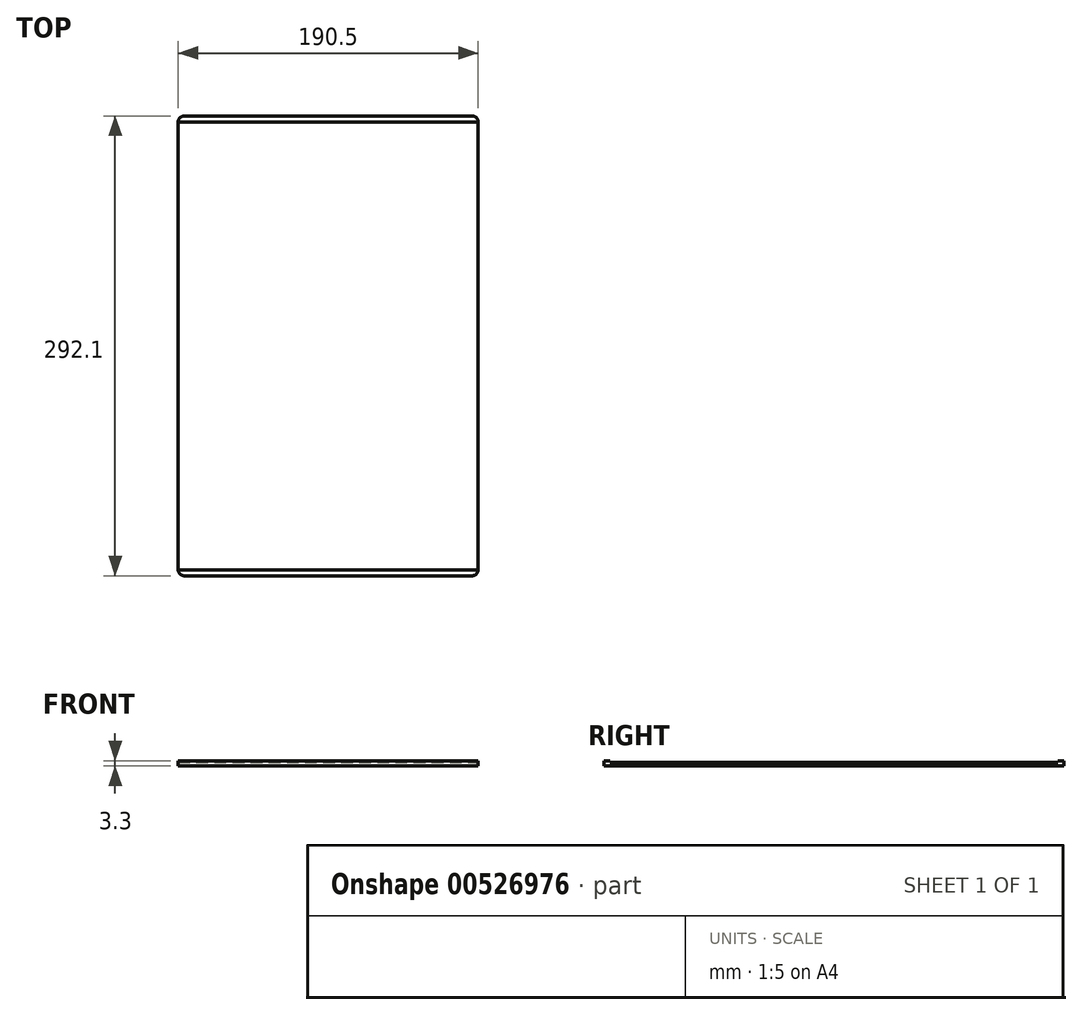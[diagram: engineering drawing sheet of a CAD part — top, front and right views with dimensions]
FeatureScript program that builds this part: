
annotation { "Feature Type Name" : "Feature", "Feature Type Description" : "" }
export const myFeature = defineFeature(function(context is Context, id is Id, definition is map)
    precondition{}
    {
        {
            var Q0;
            Q0=qCreatedBy(makeId("Top.planeOp"),FACE);
            var sketch = newSketch(context, id + "F0", { "sketchPlane" : qUnion([Q0])});
            skLineSegment(sketch, "E0.bottom", {"start": v(-91.44, 146.05) * mm, "end": v(91.44, 146.05) * mm});
            skLineSegment(sketch, "E0.top", {"start": v(-91.44, -146.05) * mm, "end": v(91.44, -146.05) * mm});
            skLineSegment(sketch, "E0.left", {"start": v(-95.25, 142.24) * mm, "end": v(-95.25, -142.24) * mm});
            skLineSegment(sketch, "E0.right", {"start": v(95.25, 142.24) * mm, "end": v(95.25, -142.24) * mm});
            skPoint(sketch, "E0.middle", {"position": v(0, 0) * mm});
            skPoint(sketch, "E1.visualSharp", {"position": v(-95.25, 146.05) * mm});
            skArc(sketch, "E1.filletArc", {"start": v(-91.44, 146.05) * mm, "mid": v(-94.13, 144.93) * mm, "end": v(-95.25, 142.24) * mm});
            skPoint(sketch, "E2.visualSharp", {"position": v(95.25, -146.05) * mm});
            skArc(sketch, "E2.filletArc", {"start": v(91.44, -146.05) * mm, "mid": v(94.13, -144.93) * mm, "end": v(95.25, -142.24) * mm});
            skPoint(sketch, "E3.visualSharp", {"position": v(95.25, 146.05) * mm});
            skArc(sketch, "E3.filletArc", {"start": v(95.25, 142.24) * mm, "mid": v(94.13, 144.93) * mm, "end": v(91.44, 146.05) * mm});
            skPoint(sketch, "E4.visualSharp", {"position": v(-95.25, -146.05) * mm});
            skArc(sketch, "E4.filletArc", {"start": v(-95.25, -142.24) * mm, "mid": v(-94.13, -144.93) * mm, "end": v(-91.44, -146.05) * mm});
            skSolve(sketch);
        }
        {
            var Q0;
            Q0 = qSketchRegion(id + "F0", true);
            extrude(context, id + "F1", {"entities" : qUnion([Q0]), "depth" : 3.3 * mm, "offsetDistance" : 25.4 * mm});
        }
        {
            var Q0;
            Q0=makeQuery(id+"F1.opExtrude","CAP_FACE",FACE,{"disambiguationData":[OSD([sQuery(id+"F0.wireOp",EDGE,"E0.bottom"),sQuery(id+"F0.wireOp",EDGE,"E0.top"),sQuery(id+"F0.wireOp",EDGE,"E0.left"),sQuery(id+"F0.wireOp",EDGE,"E0.right"),sQuery(id+"F0.wireOp",EDGE,"E1.filletArc"),sQuery(id+"F0.wireOp",EDGE,"E2.filletArc"),sQuery(id+"F0.wireOp",EDGE,"E3.filletArc"),sQuery(id+"F0.wireOp",EDGE,"E4.filletArc")])],"isStart":false});
            var sketch = newSketch(context, id + "F2", { "sketchPlane" : qUnion([Q0])});
            skLineSegment(sketch, "E5.bottom", {"start": v(-95.25, 142.24) * mm, "end": v(95.25, 142.24) * mm});
            skLineSegment(sketch, "E5.top", {"start": v(-95.25, -142.24) * mm, "end": v(95.25, -142.24) * mm});
            skLineSegment(sketch, "E5.left", {"start": v(-95.25, 142.24) * mm, "end": v(-95.25, -142.24) * mm});
            skLineSegment(sketch, "E5.right", {"start": v(95.25, 142.24) * mm, "end": v(95.25, -142.24) * mm});
            skSolve(sketch);
        }
        {
            var Q0;
            Q0=makeQuery(id+"F2.imprint","IMPRINT",FACE,{"disambiguationData":[TD([[makeQuery(id+"F2.imprint","IMPRINT",EDGE,{"derivedFrom":sQuery(id+"F2.wireOp",EDGE,"E5.bottom")}),-1.0]])]});
            extrude(context, id + "F3", {"entities" : qUnion([Q0]), "operationType" : NewBodyOperationType.REMOVE, "oppositeDirection" : true, "depth" : 1.02 * mm, "offsetDistance" : 25.4 * mm});
        }
    });
